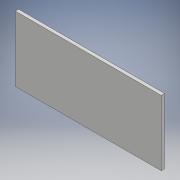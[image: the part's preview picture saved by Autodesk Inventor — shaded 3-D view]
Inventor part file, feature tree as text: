
AUTODESK INVENTOR PART (.ipt)
format: ipt  version: 2018 (Build 220112000, 112)  size: 189,440 bytes
history: native  units: mm
features: extrude x1, sketch x1
ambient origin geometry x8: Origin, YZ Plane, XZ Plane, XY Plane, X Axis, Y Axis, Z Axis, Center Point
bodies: 实体1 (feature_tree)
feature tree (2):
  extrude  "拉伸1"  Depth=1.5mm TaperAngle=0.0deg
  sketch  "草图1"  dims[d0=30.0mm d1=1.5mm d2=0.0mm d3=67.0mm]
